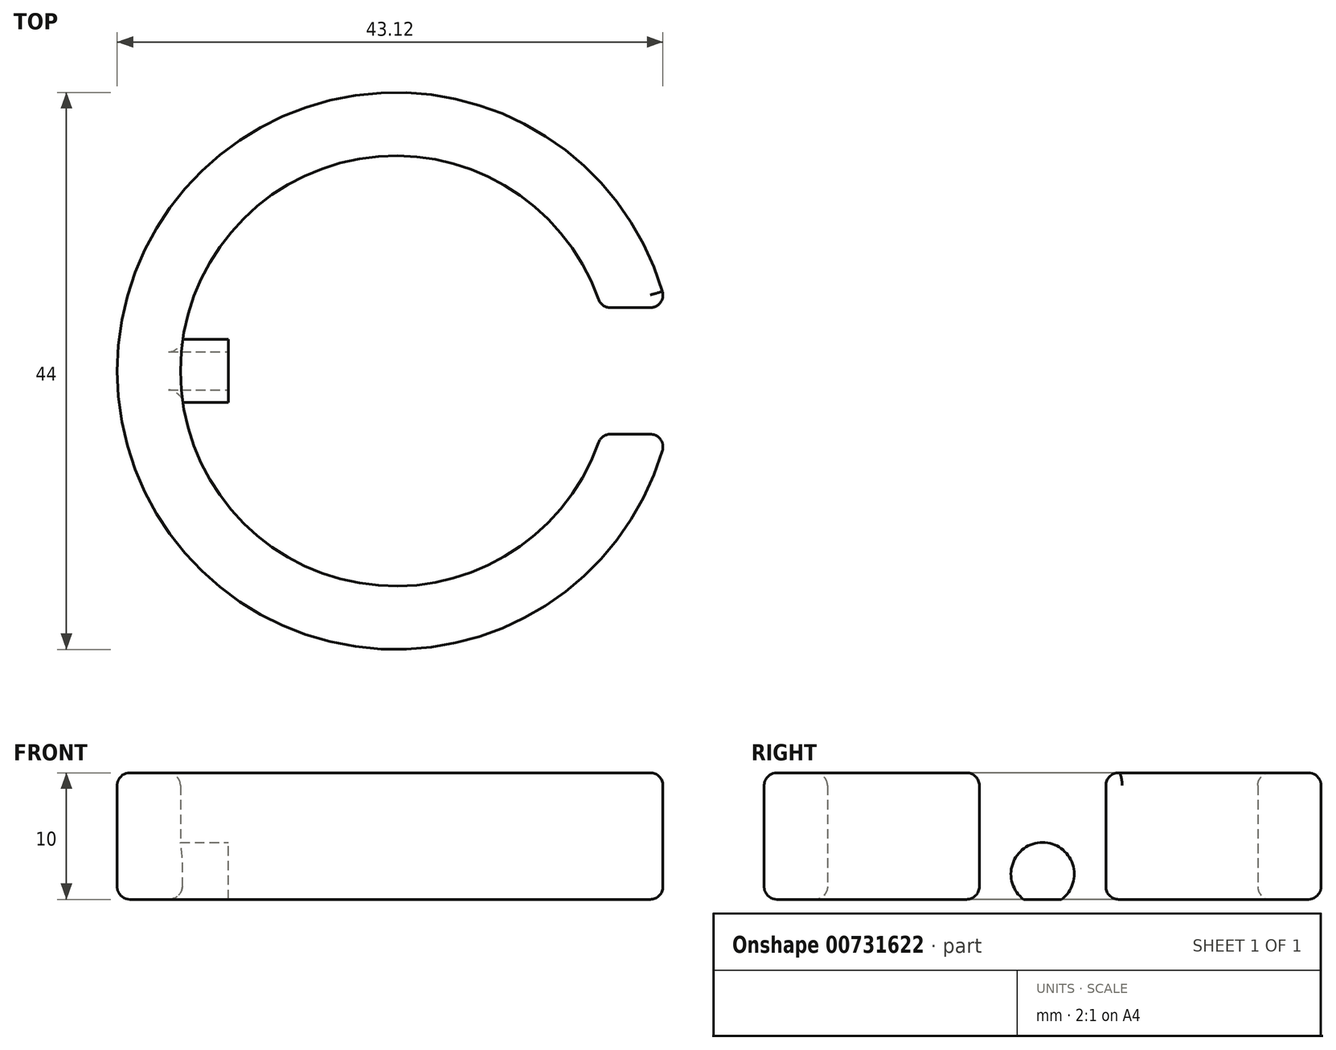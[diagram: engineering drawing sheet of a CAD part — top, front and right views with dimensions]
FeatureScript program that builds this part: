
annotation { "Feature Type Name" : "Feature", "Feature Type Description" : "" }
export const myFeature = defineFeature(function(context is Context, id is Id, definition is map)
    precondition{}
    {
        {
            var Q0;
            Q0=qCreatedBy(makeId("Top.planeOp"),FACE);
            var sketch = newSketch(context, id + "F0", { "sketchPlane" : qUnion([Q0])});
            skCircle(sketch, "E0", {"center": v(0, 0) * mm, "radius": 17 * mm});
            skCircle(sketch, "E1", {"center": v(0, 0) * mm, "radius": 22 * mm});
            skLineSegment(sketch, "E2", {"start": v(0, 0) * mm, "end": v(22, 0) * mm});
            skLineSegment(sketch, "E3.bottom", {"start": v(24.44, 5) * mm, "end": v(-2.44, 5) * mm});
            skLineSegment(sketch, "E3.top", {"start": v(24.44, -5) * mm, "end": v(-2.44, -5) * mm});
            skLineSegment(sketch, "E3.left", {"start": v(24.44, 5) * mm, "end": v(24.44, -5) * mm});
            skLineSegment(sketch, "E3.right", {"start": v(-2.44, 5) * mm, "end": v(-2.44, -5) * mm});
            skPoint(sketch, "E3.middle", {"position": v(11, 0) * mm});
            skSolve(sketch);
        }
        {
            var Q0;
            {var subQ0=sQuery(id+"F0.wireOp",EDGE,"E3.bottom");var subQ1=sQuery(id+"F0.wireOp",EDGE,"E0");var subQ2=makeQuery(id+"F0.imprint","INTERSECT",VERTEX,{"derivedFrom":[subQ1,subQ0]});Q0=makeQuery(id+"F0.imprint","IMPRINT",FACE,{"disambiguationData":[TD([[makeQuery(id+"F0.imprint","IMPRINT",EDGE,{"disambiguationData":[TD([[subQ2,-1.0]])],"derivedFrom":subQ1}),-1.0]])]});}
            extrude(context, id + "F1", {"entities" : qUnion([Q0]), "depth" : 10 * mm, "offsetDistance" : 25 * mm});
        }
        {
            var Q0;
            Q0=qCreatedBy(makeId("Right.planeOp"),FACE);
            var sketch = newSketch(context, id + "F2", { "sketchPlane" : qUnion([Q0])});
            skCircle(sketch, "E4", {"center": v(0, 2) * mm, "radius": 2.5 * mm});
            skLineSegment(sketch, "E5", {"start": v(-1.5, 0) * mm, "end": v(1.5, 0) * mm});
            skSolve(sketch);
        }
        {
            var Q0;
            {var subQ0=sQuery(id+"F2.wireOp",EDGE,"E5");Q0=makeQuery(id+"F2.imprint","IMPRINT",FACE,{"disambiguationData":[TD([[makeQuery(id+"F2.imprint","IMPRINT",EDGE,{"derivedFrom":subQ0}),1.0]])]});}
            extrude(context, id + "F3", {"entities" : qUnion([Q0]), "operationType" : NewBodyOperationType.ADD, "endBound" : BoundingType.UP_TO_NEXT, "oppositeDirection" : true, "depth" : 25 * mm, "offsetDistance" : 25 * mm});
        }
        {
            var Q0;
            Q0=makeQuery(id+"F3.opExtrude","CAP_FACE",FACE,{"disambiguationData":[OSD([sQuery(id+"F2.wireOp",EDGE,"E4"),sQuery(id+"F2.wireOp",EDGE,"E5")])],"isStart":true});
            extrude(context, id + "F4", {"entities" : qUnion([Q0]), "operationType" : NewBodyOperationType.REMOVE, "oppositeDirection" : true, "depth" : 13.2 * mm, "offsetDistance" : 25 * mm});
        }
        {
            var Q0;
            Q0=makeQuery(id+"F4.boolean.opBoolean","COPY",EDGE,{"derivedFrom":makeQuery(id+"F4.opExtrude","CAP_EDGE",EDGE,{"disambiguationData":[OSD([sQuery(id+"F2.wireOp",EDGE,"E4")])],"isStart":false})});
            var Q1;
            Q1=makeQuery(id+"F1.opExtrude","CAP_EDGE",EDGE,{"disambiguationData":[OSD([sQuery(id+"F0.wireOp",EDGE,"E0")])],"isStart":false});
            var Q2;
            Q2=makeQuery(id+"F1.opExtrude","CAP_EDGE",EDGE,{"disambiguationData":[OSD([sQuery(id+"F0.wireOp",EDGE,"E1")])],"isStart":false});
            var Q3;
            Q3=makeQuery(id+"F1.opExtrude","CAP_EDGE",EDGE,{"disambiguationData":[OSD([sQuery(id+"F0.wireOp",EDGE,"E1")])],"isStart":true});
            var Q4;
            Q4=makeQuery(id+"F1.opExtrude","SWEPT_EDGE",EDGE,{"disambiguationData":[OSD([sQuery(id+"F0.wireOp",EDGE,"E1"),sQuery(id+"F0.wireOp",EDGE,"E3.top")])]});
            var Q5;
            Q5=makeQuery(id+"F1.opExtrude","SWEPT_EDGE",EDGE,{"disambiguationData":[OSD([sQuery(id+"F0.wireOp",EDGE,"E1"),sQuery(id+"F0.wireOp",EDGE,"E3.bottom")])]});
            var Q6;
            Q6=makeQuery(id+"F1.opExtrude","SWEPT_EDGE",EDGE,{"disambiguationData":[OSD([sQuery(id+"F0.wireOp",EDGE,"E0"),sQuery(id+"F0.wireOp",EDGE,"E3.bottom")])]});
            var Q7;
            Q7=makeQuery(id+"F1.opExtrude","SWEPT_EDGE",EDGE,{"disambiguationData":[OSD([sQuery(id+"F0.wireOp",EDGE,"E0"),sQuery(id+"F0.wireOp",EDGE,"E3.top")])]});
            var Q8;
            {var subQ0=sQuery(id+"F0.wireOp",EDGE,"E3.top");var subQ1=sQuery(id+"F0.wireOp",EDGE,"E0");Q8=makeQuery(id+"F3.boolean.opBoolean","SPLIT",EDGE,{"disambiguationData":[TD([makeQuery(id+"F1.opExtrude","SWEPT_FACE",FACE,{"disambiguationData":[OSD([subQ0])]})])],"derivedFrom":makeQuery(id+"F1.opExtrude","CAP_EDGE",EDGE,{"disambiguationData":[OSD([subQ1])],"isStart":true})});}
            var Q9;
            {var subQ0=sQuery(id+"F0.wireOp",EDGE,"E3.bottom");var subQ1=sQuery(id+"F0.wireOp",EDGE,"E0");Q9=makeQuery(id+"F3.boolean.opBoolean","SPLIT",EDGE,{"disambiguationData":[TD([makeQuery(id+"F1.opExtrude","SWEPT_FACE",FACE,{"disambiguationData":[OSD([subQ0])]})])],"derivedFrom":makeQuery(id+"F1.opExtrude","CAP_EDGE",EDGE,{"disambiguationData":[OSD([subQ1])],"isStart":true})});}
            var Q10;
            Q10=makeQuery(id+"F1.opExtrude","CAP_EDGE",EDGE,{"disambiguationData":[OSD([sQuery(id+"F0.wireOp",EDGE,"E3.top")])],"isStart":false});
            var Q11;
            Q11=makeQuery(id+"F1.opExtrude","CAP_EDGE",EDGE,{"disambiguationData":[OSD([sQuery(id+"F0.wireOp",EDGE,"E3.bottom")])],"isStart":false});
            var Q12;
            Q12=makeQuery(id+"F1.opExtrude","CAP_EDGE",EDGE,{"disambiguationData":[OSD([sQuery(id+"F0.wireOp",EDGE,"E3.bottom")])],"isStart":true});
            var Q13;
            Q13=makeQuery(id+"F1.opExtrude","CAP_EDGE",EDGE,{"disambiguationData":[OSD([sQuery(id+"F0.wireOp",EDGE,"E3.top")])],"isStart":true});
            fillet(context, id + "F5", {"entities" : qUnion([Q0, Q1, Q2, Q3, Q4, Q5, Q6, Q7, Q8, Q9, Q10, Q11, Q12, Q13]), "radius" : 1 * mm, "tangentPropagation" : true, "allowEdgeOverflow" : false});
        }
    });
